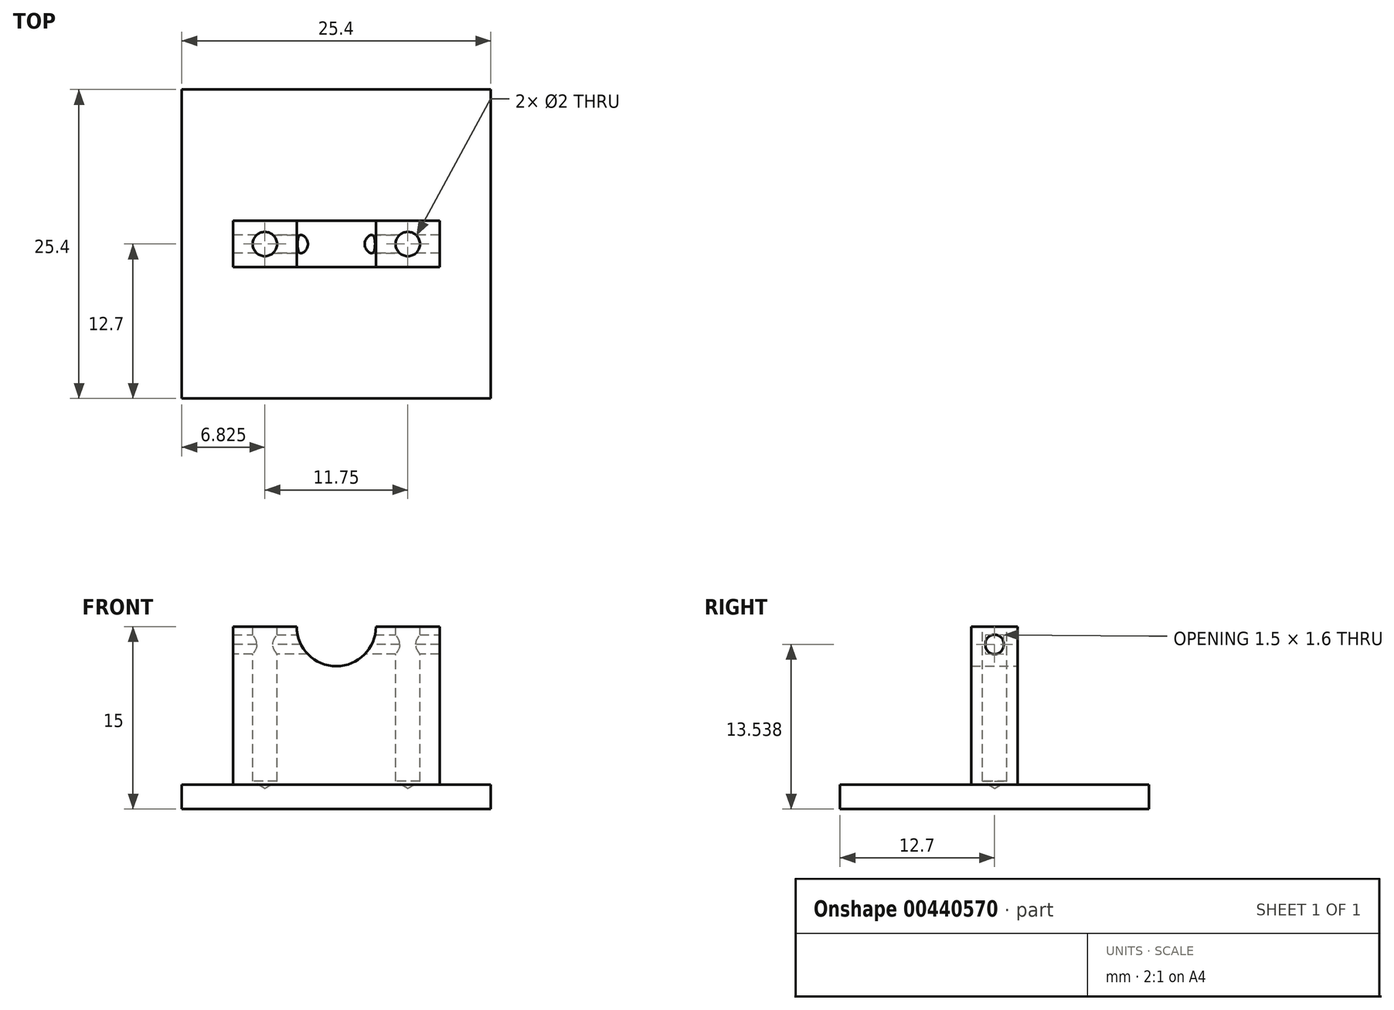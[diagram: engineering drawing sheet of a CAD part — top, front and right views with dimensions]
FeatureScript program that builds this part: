
annotation { "Feature Type Name" : "Feature", "Feature Type Description" : "" }
export const myFeature = defineFeature(function(context is Context, id is Id, definition is map)
    precondition{}
    {
        {
            var Q0;
            Q0=qCreatedBy(makeId("Top.planeOp"),FACE);
            var sketch = newSketch(context, id + "F0", { "sketchPlane" : qUnion([Q0])});
            skLineSegment(sketch, "E0.bottom", {"start": v(-12.7, 12.7) * mm, "end": v(12.7, 12.7) * mm});
            skLineSegment(sketch, "E0.top", {"start": v(-12.7, -12.7) * mm, "end": v(12.7, -12.7) * mm});
            skLineSegment(sketch, "E0.left", {"start": v(-12.7, 12.7) * mm, "end": v(-12.7, -12.7) * mm});
            skLineSegment(sketch, "E0.right", {"start": v(12.7, 12.7) * mm, "end": v(12.7, -12.7) * mm});
            skSolve(sketch);
        }
        {
            var Q0;
            Q0=makeQuery(id+"F0.imprint","IMPRINT",FACE,{"disambiguationData":[TD([[makeQuery(id+"F0.imprint","IMPRINT",EDGE,{"derivedFrom":sQuery(id+"F0.wireOp",EDGE,"E0.bottom")}),-1.0]])]});
            extrude(context, id + "F1", {"entities" : qUnion([Q0]), "depth" : 2 * mm});
        }
        {
            var Q0;
            Q0=qCreatedBy(makeId("Front.planeOp"),FACE);
            var sketch = newSketch(context, id + "F2", { "sketchPlane" : qUnion([Q0])});
            skLineSegment(sketch, "E1.bottom", {"start": v(-8.5, 0) * mm, "end": v(8.5, 0) * mm});
            skLineSegment(sketch, "E1.top", {"start": v(-8.5, 15) * mm, "end": v(8.5, 15) * mm});
            skLineSegment(sketch, "E1.left", {"start": v(-8.5, 0) * mm, "end": v(-8.5, 15) * mm});
            skLineSegment(sketch, "E1.right", {"start": v(8.5, 0) * mm, "end": v(8.5, 15) * mm});
            skPoint(sketch, "E2", {"position": v(0, 15) * mm});
            skSolve(sketch);
        }
        {
            var Q0;
            Q0=makeQuery(id+"F2.imprint","IMPRINT",FACE,{"disambiguationData":[TD([[makeQuery(id+"F2.imprint","IMPRINT",EDGE,{"derivedFrom":sQuery(id+"F2.wireOp",EDGE,"E1.bottom")}),1.0]])]});
            extrude(context, id + "F3", {"entities" : qUnion([Q0]), "operationType" : NewBodyOperationType.ADD, "depth" : 3.8 * mm, "symmetric" : true});
        }
        {
            var Q0;
            Q0=qCreatedBy(makeId("Front.planeOp"),FACE);
            var sketch = newSketch(context, id + "F4", { "sketchPlane" : qUnion([Q0])});
            skCircle(sketch, "E3", {"center": v(0, 15) * mm, "radius": 3.25 * mm});
            skSolve(sketch);
        }
        {
            var Q0;
            Q0=makeQuery(id+"F4.imprint","IMPRINT",FACE,{"disambiguationData":[TD([[makeQuery(id+"F4.imprint","IMPRINT",EDGE,{"derivedFrom":sQuery(id+"F4.wireOp",EDGE,"E3")}),1.0]])]});
            extrude(context, id + "F5", {"entities" : qUnion([Q0]), "operationType" : NewBodyOperationType.REMOVE, "depth" : 5.23 * mm, "symmetric" : true});
        }
        {
            var Q0;
            {var subQ1=sQuery(id+"F2.wireOp",EDGE,"E1.left");var subQ2=sQuery(id+"F2.wireOp",EDGE,"E1.top");Q0=makeQuery(id+"F5.boolean.opBoolean","SPLIT",FACE,{"disambiguationData":[TD([makeQuery(id+"F3.opExtrude","SWEPT_FACE",FACE,{"disambiguationData":[OSD([subQ1])]})])],"derivedFrom":makeQuery(id+"F3.opExtrude","SWEPT_FACE",FACE,{"disambiguationData":[OSD([subQ2])]})});}
            var sketch = newSketch(context, id + "F6", { "sketchPlane" : qUnion([Q0])});
            skCircle(sketch, "E4", {"center": v(-5.87, 0) * mm, "radius": 0.62 * mm});
            skCircle(sketch, "E5", {"center": v(5.88, 0) * mm, "radius": 0.62 * mm});
            skSolve(sketch);
        }
        {
            var Q0;
            Q0=sQuery(id+"F6.wireOp",VERTEX,"E5.center");
            var Q1;
            Q1=sQuery(id+"F6.wireOp",VERTEX,"E4.center");
            var Q2;
            Q2=makeQuery(id+"F1.opExtrude","SWEPT_BODY",BODY,{"disambiguationData":[OSD([sQuery(id+"F0.wireOp",EDGE,"E0.bottom"),sQuery(id+"F0.wireOp",EDGE,"E0.top"),sQuery(id+"F0.wireOp",EDGE,"E0.left"),sQuery(id+"F0.wireOp",EDGE,"E0.right")])]});
            hole(context, id + "F7", {"style" : HoleStyle.SIMPLE, "endStyle" : HoleEndStyle.BLIND, "holeDiameter" : 2 * mm, "holeDepth" : 12.7 * mm, "isTappedThrough" : true, "tappedDepth" : 12.7 * mm, "tapClearance" : 3, "locations" : qUnion([Q0, Q1]), "scope" : qUnion([Q2])});
        }
        {
            var Q0;
            Q0=makeQuery(id+"F3.opExtrude","SWEPT_FACE",FACE,{"disambiguationData":[OSD([sQuery(id+"F2.wireOp",EDGE,"E1.left")])]});
            var sketch = newSketch(context, id + "F8", { "sketchPlane" : qUnion([Q0])});
            skCircle(sketch, "E6", {"center": v(0, 13.49) * mm, "radius": 1.23 * mm});
            skSolve(sketch);
        }
        {
            var Q0;
            Q0=makeQuery(id+"F3.opExtrude","SWEPT_FACE",FACE,{"disambiguationData":[OSD([sQuery(id+"F2.wireOp",EDGE,"E1.right")])]});
            var sketch = newSketch(context, id + "F9", { "sketchPlane" : qUnion([Q0])});
            skCircle(sketch, "E7", {"center": v(0, 13.59) * mm, "radius": 1.2 * mm});
            skSolve(sketch);
        }
        {
            var Q0;
            Q0=sQuery(id+"F9.wireOp",VERTEX,"E7.center");
            var Q1;
            Q1=sQuery(id+"F8.wireOp",VERTEX,"E6.center");
            var Q2;
            Q2=makeQuery(id+"F1.opExtrude","SWEPT_BODY",BODY,{"disambiguationData":[OSD([sQuery(id+"F0.wireOp",EDGE,"E0.bottom"),sQuery(id+"F0.wireOp",EDGE,"E0.top"),sQuery(id+"F0.wireOp",EDGE,"E0.left"),sQuery(id+"F0.wireOp",EDGE,"E0.right")])]});
            hole(context, id + "F10", {"style" : HoleStyle.SIMPLE, "endStyle" : HoleEndStyle.THROUGH, "holeDiameter" : 1.5 * mm, "isTappedThrough" : true, "tappedDepth" : 12.7 * mm, "tapClearance" : 3, "locations" : qUnion([Q0, Q1]), "scope" : qUnion([Q2])});
        }
    });
